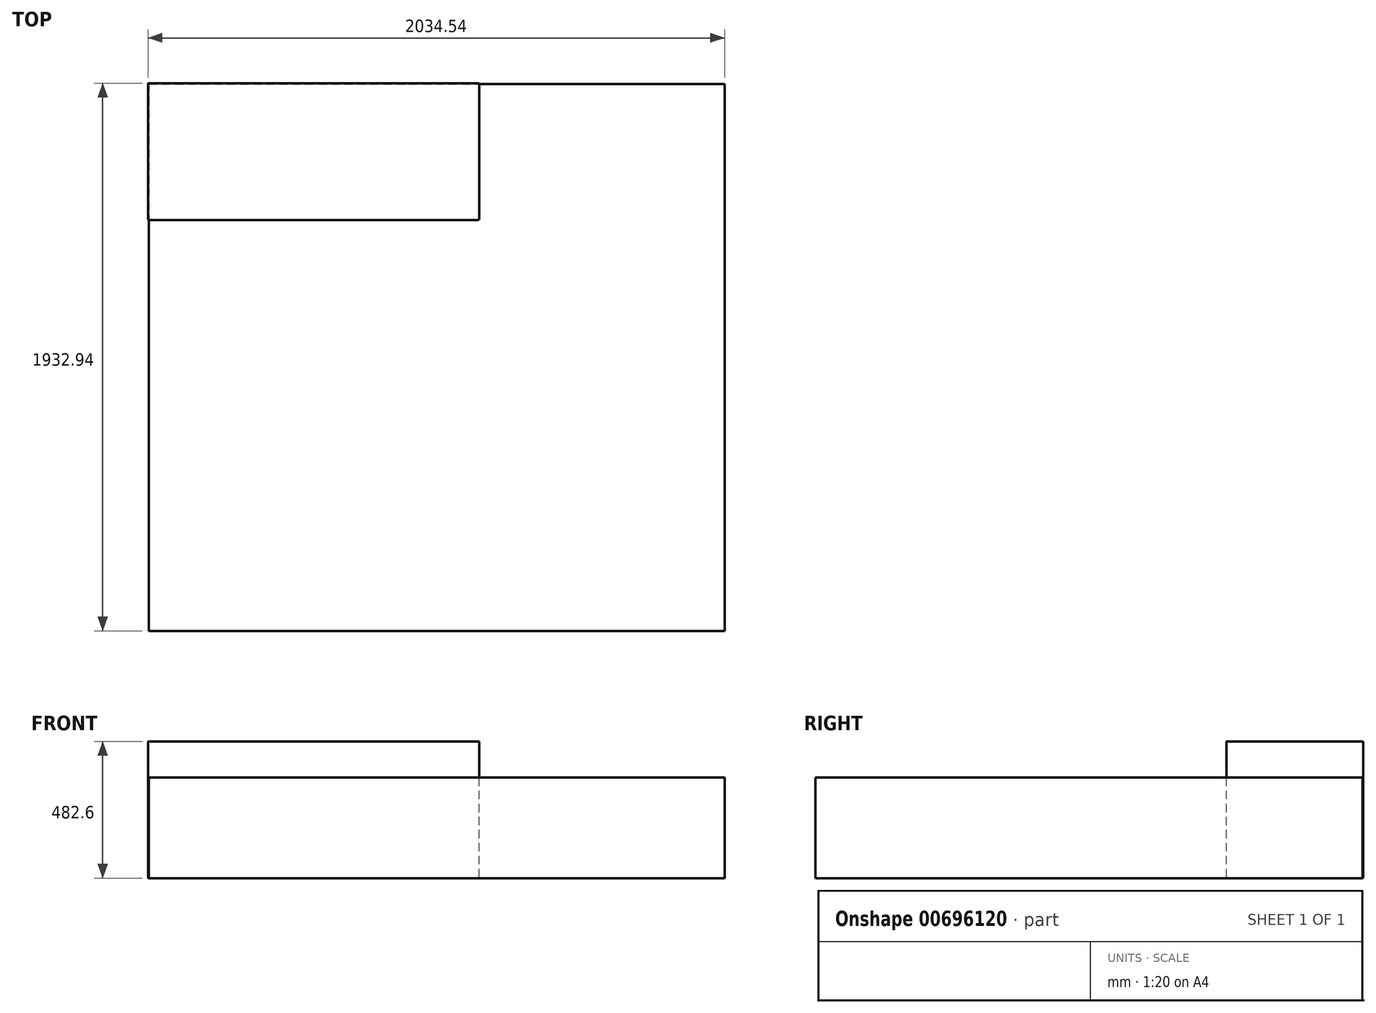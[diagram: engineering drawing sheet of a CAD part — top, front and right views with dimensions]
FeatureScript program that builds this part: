
annotation { "Feature Type Name" : "Feature", "Feature Type Description" : "" }
export const myFeature = defineFeature(function(context is Context, id is Id, definition is map)
    precondition{}
    {
        {
            var Q0;
            Q0=qCreatedBy(makeId("Front.planeOp"),FACE);
            var sketch = newSketch(context, id + "F0", { "sketchPlane" : qUnion([Q0])});
            skLineSegment(sketch, "E0.bottom", {"start": v(-584.2, 0) * mm, "end": v(584.2, 0) * mm});
            skLineSegment(sketch, "E0.top", {"start": v(-584.2, 482.6) * mm, "end": v(584.2, 482.6) * mm});
            skLineSegment(sketch, "E0.left", {"start": v(-584.2, 0) * mm, "end": v(-584.2, 482.6) * mm});
            skLineSegment(sketch, "E0.right", {"start": v(584.2, 0) * mm, "end": v(584.2, 482.6) * mm});
            skSolve(sketch);
        }
        {
            var Q0;
            Q0=makeQuery(id+"F0.imprint","IMPRINT",FACE,{"disambiguationData":[TD([[makeQuery(id+"F0.imprint","IMPRINT",EDGE,{"derivedFrom":sQuery(id+"F0.wireOp",EDGE,"E0.bottom")}),1.0]])]});
            extrude(context, id + "F1", {"entities" : qUnion([Q0]), "endBound" : BoundingType.SYMMETRIC, "depth" : 482.6 * mm, "offsetDistance" : 25.4 * mm});
        }
        {
            var Q0;
            Q0=makeQuery(id+"F1.opExtrude","CAP_EDGE",EDGE,{"disambiguationData":[OSD([sQuery(id+"F0.wireOp",EDGE,"E0.top")])],"isStart":false});
            var Q1;
            Q1=makeQuery(id+"F1.opExtrude","CAP_EDGE",EDGE,{"disambiguationData":[OSD([sQuery(id+"F0.wireOp",EDGE,"E0.bottom")])],"isStart":false});
            var Q2;
            Q2=makeQuery(id+"F1.opExtrude","CAP_EDGE",EDGE,{"disambiguationData":[OSD([sQuery(id+"F0.wireOp",EDGE,"E0.top")])],"isStart":true});
            var Q3;
            Q3=makeQuery(id+"F1.opExtrude","CAP_EDGE",EDGE,{"disambiguationData":[OSD([sQuery(id+"F0.wireOp",EDGE,"E0.bottom")])],"isStart":true});
            var Q4;
            Q4=makeQuery(id+"F1.opExtrude","SWEPT_FACE",FACE,{"disambiguationData":[OSD([sQuery(id+"F0.wireOp",EDGE,"E0.right")])]});
            var Q5;
            Q5=makeQuery(id+"F1.opExtrude","SWEPT_FACE",FACE,{"disambiguationData":[OSD([sQuery(id+"F0.wireOp",EDGE,"E0.left")])]});
            fillet(context, id + "F2", {"entities" : qUnion([Q0, Q1, Q2, Q3, Q4, Q5]), "radius" : 2.54 * mm, "tangentPropagation" : true, "allowEdgeOverflow" : false});
        }
        {
            var Q0;
            Q0=qCreatedBy(makeId("Top.planeOp"),FACE);
            var sketch = newSketch(context, id + "F3", { "sketchPlane" : qUnion([Q0])});
            skLineSegment(sketch, "E1.bottom", {"start": v(-581.66, 238.76) * mm, "end": v(1450.34, 238.76) * mm});
            skLineSegment(sketch, "E1.top", {"start": v(-581.66, -1691.64) * mm, "end": v(1450.34, -1691.64) * mm});
            skLineSegment(sketch, "E1.left", {"start": v(-581.66, 238.76) * mm, "end": v(-581.66, -1691.64) * mm});
            skLineSegment(sketch, "E1.right", {"start": v(1450.34, 238.76) * mm, "end": v(1450.34, -1691.64) * mm});
            skSolve(sketch);
        }
        {
            var Q0;
            Q0=makeQuery(id+"F3.imprint","IMPRINT",FACE,{"disambiguationData":[TD([[makeQuery(id+"F3.imprint","IMPRINT",EDGE,{"derivedFrom":sQuery(id+"F3.wireOp",EDGE,"E1.bottom")}),-1.0]])]});
            extrude(context, id + "F4", {"entities" : qUnion([Q0]), "depth" : 355.6 * mm, "offsetDistance" : 25.4 * mm});
        }
    });
